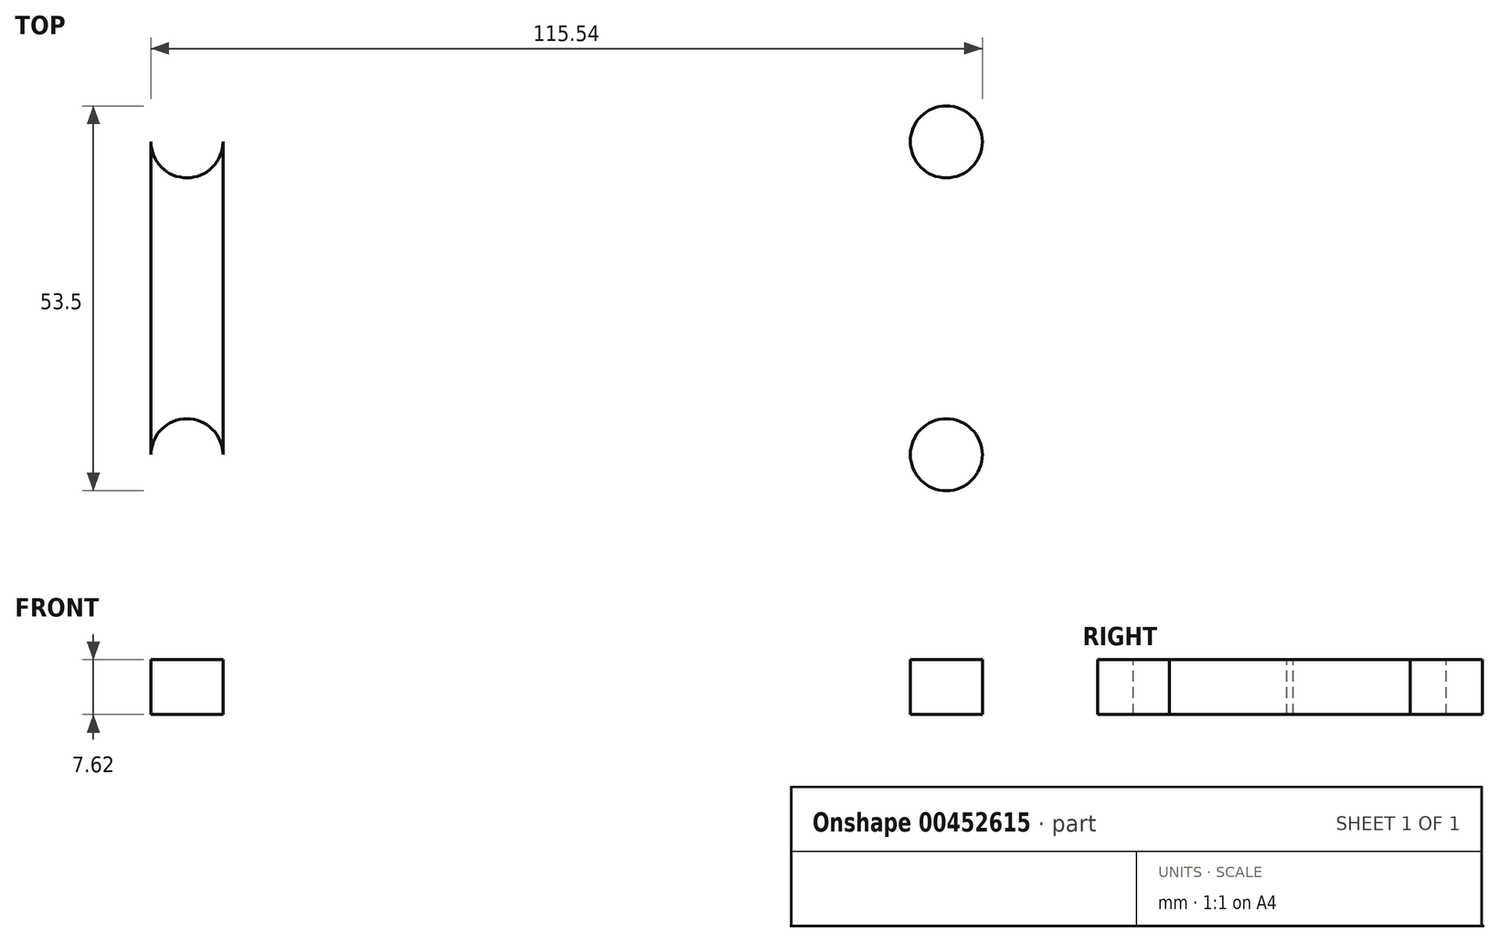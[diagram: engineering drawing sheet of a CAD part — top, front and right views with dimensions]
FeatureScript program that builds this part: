
annotation { "Feature Type Name" : "Feature", "Feature Type Description" : "" }
export const myFeature = defineFeature(function(context is Context, id is Id, definition is map)
    precondition{}
    {
        {
            var Q0;
            Q0=qCreatedBy(makeId("Top.planeOp"),FACE);
            var sketch = newSketch(context, id + "F0", { "sketchPlane" : qUnion([Q0])});
            skLineSegment(sketch, "E0.bottom", {"start": v(63.25, -31.75) * mm, "end": v(-63.25, -31.75) * mm});
            skLineSegment(sketch, "E0.top", {"start": v(63.25, 31.75) * mm, "end": v(-63.25, 31.75) * mm});
            skLineSegment(sketch, "E0.left", {"start": v(63.25, -31.75) * mm, "end": v(63.25, 31.75) * mm});
            skLineSegment(sketch, "E0.right", {"start": v(-63.25, -31.75) * mm, "end": v(-63.25, 31.75) * mm});
            skPoint(sketch, "E0.middle", {"position": v(0, 0) * mm});
            skLineSegment(sketch, "E1", {"start": v(0, 31.75) * mm, "end": v(0, -31.75) * mm, "construction": true});
            skLineSegment(sketch, "E2", {"start": v(-63.25, 0) * mm, "end": v(63.25, 0) * mm, "construction": true});
            skCircle(sketch, "E3", {"center": v(-27.5, 27.5) * mm, "radius": 2 * mm});
            skCircle(sketch, "E4.0.1.0", {"center": v(-27.5, -27.5) * mm, "radius": 2 * mm});
            skCircle(sketch, "E4.1.0.0", {"center": v(27.5, 27.5) * mm, "radius": 2 * mm});
            skCircle(sketch, "E4.1.1.0", {"center": v(27.5, -27.5) * mm, "radius": 2 * mm});
            skLineSegment(sketch, "E4.direction1", {"start": v(-27.5, 27.5) * mm, "end": v(27.5, 27.5) * mm, "construction": true});
            skLineSegment(sketch, "E4.direction2", {"start": v(-27.5, 27.5) * mm, "end": v(-27.5, -27.5) * mm, "construction": true});
            skCircle(sketch, "E5", {"center": v(0, 0) * mm, "radius": 26.94 * mm});
            skCircle(sketch, "E6", {"center": v(-62.75, 0) * mm, "radius": 5 * mm});
            skCircle(sketch, "E7", {"center": v(62.75, 0) * mm, "radius": 5 * mm});
            skCircle(sketch, "E8", {"center": v(-62.75, 0) * mm, "radius": 120.5 * mm});
            skCircle(sketch, "E9", {"center": v(-62.75, 0) * mm, "radius": 130.5 * mm});
            skCircle(sketch, "E10", {"center": v(-62.75, 0) * mm, "radius": 125.5 * mm});
            skCircle(sketch, "E11", {"center": v(60.77, 22.22) * mm, "radius": 5 * mm});
            skCircle(sketch, "E12", {"center": v(60.43, -24.02) * mm, "radius": 5 * mm});
            skCircle(sketch, "E13", {"center": v(-27.5, 27.5) * mm, "radius": 3.5 * mm});
            skCircle(sketch, "E14.MirrorC", {"center": v(27.5, 27.5) * mm, "radius": 3.5 * mm});
            skCircle(sketch, "E15.MirrorC", {"center": v(-27.5, -27.5) * mm, "radius": 3.5 * mm});
            skCircle(sketch, "E16.MirrorC", {"center": v(27.5, -27.5) * mm, "radius": 3.5 * mm});
            skSolve(sketch);
        }
        {
            var Q0;
            {var subQ0=sQuery(id+"F0.wireOp",EDGE,"E6");var subQ1=sQuery(id+"F0.wireOp",EDGE,"E0.right");var subQ2=makeQuery(id+"F0.imprint","INTERSECT",VERTEX,{"disambiguationData":[OD(0.0)],"derivedFrom":[subQ1,subQ0]});Q0=makeQuery(id+"F0.imprint","IMPRINT",FACE,{"disambiguationData":[TD([[makeQuery(id+"F0.imprint","IMPRINT",EDGE,{"disambiguationData":[TD([[subQ2,-1.0]])],"derivedFrom":subQ1}),-1.0]])]});}
            var Q1;
            {var subQ0=sQuery(id+"F0.wireOp",EDGE,"E6");var subQ1=sQuery(id+"F0.wireOp",EDGE,"E0.right");var subQ2=makeQuery(id+"F0.imprint","INTERSECT",VERTEX,{"disambiguationData":[OD(0.0)],"derivedFrom":[subQ1,subQ0]});Q1=makeQuery(id+"F0.imprint","IMPRINT",FACE,{"disambiguationData":[TD([[makeQuery(id+"F0.imprint","IMPRINT",EDGE,{"disambiguationData":[TD([[subQ2,-1.0]])],"derivedFrom":subQ1}),-1.0]])]});}
            var Q2;
            {var subQ0=sQuery(id+"F0.wireOp",EDGE,"E10");var subQ1=sQuery(id+"F0.wireOp",EDGE,"E0.top");var subQ2=makeQuery(id+"F0.imprint","INTERSECT",VERTEX,{"derivedFrom":[subQ1,subQ0]});Q2=makeQuery(id+"F0.imprint","IMPRINT",FACE,{"disambiguationData":[TD([[makeQuery(id+"F0.imprint","IMPRINT",EDGE,{"disambiguationData":[TD([[subQ2,-1.0]])],"derivedFrom":subQ1}),1.0]])]});}
            var Q3;
            {var subQ0=sQuery(id+"F0.wireOp",EDGE,"E0.left");var subQ1=sQuery(id+"F0.wireOp",EDGE,"E0.top");var subQ2=makeQuery(id+"F0.imprint","INTERSECT",VERTEX,{"derivedFrom":[subQ1,subQ0]});Q3=makeQuery(id+"F0.imprint","IMPRINT",FACE,{"disambiguationData":[TD([[makeQuery(id+"F0.imprint","IMPRINT",EDGE,{"disambiguationData":[TD([[subQ2,-1.0]])],"derivedFrom":subQ1}),1.0]])]});}
            var Q4;
            {var subQ0=sQuery(id+"F0.wireOp",EDGE,"E10");var subQ1=sQuery(id+"F0.wireOp",EDGE,"E0.top");var subQ2=makeQuery(id+"F0.imprint","INTERSECT",VERTEX,{"derivedFrom":[subQ1,subQ0]});Q4=makeQuery(id+"F0.imprint","IMPRINT",FACE,{"disambiguationData":[TD([[makeQuery(id+"F0.imprint","IMPRINT",EDGE,{"disambiguationData":[TD([[subQ2,-1.0]])],"derivedFrom":subQ1}),1.0]])]});}
            var Q5;
            {var subQ0=sQuery(id+"F0.wireOp",EDGE,"E0.left");var subQ1=sQuery(id+"F0.wireOp",EDGE,"E0.bottom");var subQ2=makeQuery(id+"F0.imprint","INTERSECT",VERTEX,{"derivedFrom":[subQ1,subQ0]});Q5=makeQuery(id+"F0.imprint","IMPRINT",FACE,{"disambiguationData":[TD([[makeQuery(id+"F0.imprint","IMPRINT",EDGE,{"disambiguationData":[TD([[subQ2,-1.0]])],"derivedFrom":subQ1}),-1.0]])]});}
            var Q6;
            {var subQ0=sQuery(id+"F0.wireOp",EDGE,"E0.left");var subQ1=sQuery(id+"F0.wireOp",EDGE,"E0.top");var subQ2=makeQuery(id+"F0.imprint","INTERSECT",VERTEX,{"derivedFrom":[subQ1,subQ0]});Q6=makeQuery(id+"F0.imprint","IMPRINT",FACE,{"disambiguationData":[TD([[makeQuery(id+"F0.imprint","IMPRINT",EDGE,{"disambiguationData":[TD([[subQ2,-1.0]])],"derivedFrom":subQ1}),1.0]])]});}
            var Q7;
            {var subQ0=sQuery(id+"F0.wireOp",EDGE,"E12");var subQ1=sQuery(id+"F0.wireOp",EDGE,"E0.left");var subQ2=makeQuery(id+"F0.imprint","INTERSECT",VERTEX,{"disambiguationData":[OD(0.0)],"derivedFrom":[subQ1,subQ0]});Q7=makeQuery(id+"F0.imprint","IMPRINT",FACE,{"disambiguationData":[TD([[makeQuery(id+"F0.imprint","IMPRINT",EDGE,{"disambiguationData":[TD([[subQ2,-1.0]])],"derivedFrom":subQ1}),1.0]])]});}
            var Q8;
            {var subQ0=sQuery(id+"F0.wireOp",EDGE,"E12");var subQ1=sQuery(id+"F0.wireOp",EDGE,"E0.left");var subQ2=makeQuery(id+"F0.imprint","INTERSECT",VERTEX,{"disambiguationData":[OD(1.0)],"derivedFrom":[subQ1,subQ0]});Q8=makeQuery(id+"F0.imprint","IMPRINT",FACE,{"disambiguationData":[TD([[makeQuery(id+"F0.imprint","IMPRINT",EDGE,{"disambiguationData":[TD([[subQ2,-1.0]])],"derivedFrom":subQ1}),1.0]])]});}
            var Q9;
            {var subQ0=sQuery(id+"F0.wireOp",EDGE,"E7");var subQ1=sQuery(id+"F0.wireOp",EDGE,"E0.left");var subQ2=makeQuery(id+"F0.imprint","INTERSECT",VERTEX,{"disambiguationData":[OD(0.0)],"derivedFrom":[subQ1,subQ0]});Q9=makeQuery(id+"F0.imprint","IMPRINT",FACE,{"disambiguationData":[TD([[makeQuery(id+"F0.imprint","IMPRINT",EDGE,{"disambiguationData":[TD([[subQ2,-1.0]])],"derivedFrom":subQ1}),1.0]])]});}
            var Q10;
            {var subQ0=sQuery(id+"F0.wireOp",EDGE,"E7");var subQ1=sQuery(id+"F0.wireOp",EDGE,"E0.left");var subQ2=makeQuery(id+"F0.imprint","INTERSECT",VERTEX,{"disambiguationData":[OD(1.0)],"derivedFrom":[subQ1,subQ0]});Q10=makeQuery(id+"F0.imprint","IMPRINT",FACE,{"disambiguationData":[TD([[makeQuery(id+"F0.imprint","IMPRINT",EDGE,{"disambiguationData":[TD([[subQ2,-1.0]])],"derivedFrom":subQ1}),1.0]])]});}
            var Q11;
            {var subQ0=sQuery(id+"F0.wireOp",EDGE,"E11");var subQ1=sQuery(id+"F0.wireOp",EDGE,"E0.left");var subQ2=makeQuery(id+"F0.imprint","INTERSECT",VERTEX,{"disambiguationData":[OD(0.0)],"derivedFrom":[subQ1,subQ0]});Q11=makeQuery(id+"F0.imprint","IMPRINT",FACE,{"disambiguationData":[TD([[makeQuery(id+"F0.imprint","IMPRINT",EDGE,{"disambiguationData":[TD([[subQ2,-1.0]])],"derivedFrom":subQ1}),1.0]])]});}
            var Q12;
            {var subQ0=sQuery(id+"F0.wireOp",EDGE,"E0.left");var subQ1=sQuery(id+"F0.wireOp",EDGE,"E0.bottom");var subQ2=makeQuery(id+"F0.imprint","INTERSECT",VERTEX,{"derivedFrom":[subQ1,subQ0]});Q12=makeQuery(id+"F0.imprint","IMPRINT",FACE,{"disambiguationData":[TD([[makeQuery(id+"F0.imprint","IMPRINT",EDGE,{"disambiguationData":[TD([[subQ2,-1.0]])],"derivedFrom":subQ1}),-1.0]])]});}
            var Q13;
            {var subQ0=sQuery(id+"F0.wireOp",EDGE,"E10");var subQ1=sQuery(id+"F0.wireOp",EDGE,"E0.bottom");var subQ2=makeQuery(id+"F0.imprint","INTERSECT",VERTEX,{"derivedFrom":[subQ1,subQ0]});Q13=makeQuery(id+"F0.imprint","IMPRINT",FACE,{"disambiguationData":[TD([[makeQuery(id+"F0.imprint","IMPRINT",EDGE,{"disambiguationData":[TD([[subQ2,-1.0]])],"derivedFrom":subQ1}),-1.0]])]});}
            var Q14;
            {var subQ0=sQuery(id+"F0.wireOp",EDGE,"E10");var subQ1=sQuery(id+"F0.wireOp",EDGE,"E0.bottom");var subQ2=makeQuery(id+"F0.imprint","INTERSECT",VERTEX,{"derivedFrom":[subQ1,subQ0]});Q14=makeQuery(id+"F0.imprint","IMPRINT",FACE,{"disambiguationData":[TD([[makeQuery(id+"F0.imprint","IMPRINT",EDGE,{"disambiguationData":[TD([[subQ2,-1.0]])],"derivedFrom":subQ1}),-1.0]])]});}
            var Q15;
            Q15=makeQuery(id+"F0.imprint","IMPRINT",FACE,{"disambiguationData":[TD([[makeQuery(id+"F0.imprint","IMPRINT",EDGE,{"derivedFrom":sQuery(id+"F0.wireOp",EDGE,"E4.0.1.0")}),-1.0]])]});
            var Q16;
            Q16=makeQuery(id+"F0.imprint","IMPRINT",FACE,{"disambiguationData":[TD([[makeQuery(id+"F0.imprint","IMPRINT",EDGE,{"derivedFrom":sQuery(id+"F0.wireOp",EDGE,"E3")}),-1.0]])]});
            var Q17;
            Q17=makeQuery(id+"F0.imprint","IMPRINT",FACE,{"disambiguationData":[TD([[makeQuery(id+"F0.imprint","IMPRINT",EDGE,{"derivedFrom":sQuery(id+"F0.wireOp",EDGE,"E4.1.0.0")}),-1.0]])]});
            var Q18;
            Q18=makeQuery(id+"F0.imprint","IMPRINT",FACE,{"disambiguationData":[TD([[makeQuery(id+"F0.imprint","IMPRINT",EDGE,{"derivedFrom":sQuery(id+"F0.wireOp",EDGE,"E4.1.1.0")}),-1.0]])]});
            var Q19;
            {var subQ0=sQuery(id+"F0.wireOp",EDGE,"E11");var subQ1=sQuery(id+"F0.wireOp",EDGE,"E10");var subQ2=makeQuery(id+"F0.imprint","INTERSECT",VERTEX,{"disambiguationData":[OD(0.0)],"derivedFrom":[subQ1,subQ0]});Q19=makeQuery(id+"F0.imprint","IMPRINT",FACE,{"disambiguationData":[TD([[makeQuery(id+"F0.imprint","IMPRINT",EDGE,{"disambiguationData":[TD([[subQ2,-1.0]])],"derivedFrom":subQ1}),1.0]])]});}
            var Q20;
            {var subQ0=sQuery(id+"F0.wireOp",EDGE,"E11");var subQ1=sQuery(id+"F0.wireOp",EDGE,"E0.left");var subQ2=makeQuery(id+"F0.imprint","INTERSECT",VERTEX,{"disambiguationData":[OD(0.0)],"derivedFrom":[subQ1,subQ0]});Q20=makeQuery(id+"F0.imprint","IMPRINT",FACE,{"disambiguationData":[TD([[makeQuery(id+"F0.imprint","IMPRINT",EDGE,{"disambiguationData":[TD([[subQ2,-1.0]])],"derivedFrom":subQ1}),1.0]])]});}
            var Q21;
            {var subQ0=sQuery(id+"F0.wireOp",EDGE,"E10");var subQ1=sQuery(id+"F0.wireOp",EDGE,"E7");var subQ2=makeQuery(id+"F0.imprint","INTERSECT",VERTEX,{"disambiguationData":[OD(0.0)],"derivedFrom":[subQ1,subQ0]});Q21=makeQuery(id+"F0.imprint","IMPRINT",FACE,{"disambiguationData":[TD([[makeQuery(id+"F0.imprint","IMPRINT",EDGE,{"disambiguationData":[TD([[subQ2,-1.0]])],"derivedFrom":subQ1}),-1.0]])]});}
            var Q22;
            {var subQ0=sQuery(id+"F0.wireOp",EDGE,"E7");var subQ1=sQuery(id+"F0.wireOp",EDGE,"E0.left");var subQ2=makeQuery(id+"F0.imprint","INTERSECT",VERTEX,{"disambiguationData":[OD(1.0)],"derivedFrom":[subQ1,subQ0]});Q22=makeQuery(id+"F0.imprint","IMPRINT",FACE,{"disambiguationData":[TD([[makeQuery(id+"F0.imprint","IMPRINT",EDGE,{"disambiguationData":[TD([[subQ2,-1.0]])],"derivedFrom":subQ1}),1.0]])]});}
            var Q23;
            {var subQ0=sQuery(id+"F0.wireOp",EDGE,"E10");var subQ1=sQuery(id+"F0.wireOp",EDGE,"E7");var subQ2=makeQuery(id+"F0.imprint","INTERSECT",VERTEX,{"disambiguationData":[OD(0.0)],"derivedFrom":[subQ1,subQ0]});Q23=makeQuery(id+"F0.imprint","IMPRINT",FACE,{"disambiguationData":[TD([[makeQuery(id+"F0.imprint","IMPRINT",EDGE,{"disambiguationData":[TD([[subQ2,-1.0]])],"derivedFrom":subQ1}),1.0]])]});}
            var Q24;
            {var subQ0=sQuery(id+"F0.wireOp",EDGE,"E7");var subQ1=sQuery(id+"F0.wireOp",EDGE,"E0.left");var subQ2=makeQuery(id+"F0.imprint","INTERSECT",VERTEX,{"disambiguationData":[OD(0.0)],"derivedFrom":[subQ1,subQ0]});Q24=makeQuery(id+"F0.imprint","IMPRINT",FACE,{"disambiguationData":[TD([[makeQuery(id+"F0.imprint","IMPRINT",EDGE,{"disambiguationData":[TD([[subQ2,-1.0]])],"derivedFrom":subQ1}),1.0]])]});}
            var Q25;
            {var subQ0=sQuery(id+"F0.wireOp",EDGE,"E8");var subQ1=sQuery(id+"F0.wireOp",EDGE,"E7");var subQ2=makeQuery(id+"F0.imprint","INTERSECT",VERTEX,{"derivedFrom":[subQ1,subQ0]});Q25=makeQuery(id+"F0.imprint","IMPRINT",FACE,{"disambiguationData":[TD([[makeQuery(id+"F0.imprint","IMPRINT",EDGE,{"disambiguationData":[TD([[subQ2,-1.0]])],"derivedFrom":subQ1}),-1.0]])]});}
            var Q26;
            {var subQ0=sQuery(id+"F0.wireOp",EDGE,"E12");var subQ1=sQuery(id+"F0.wireOp",EDGE,"E10");var subQ2=makeQuery(id+"F0.imprint","INTERSECT",VERTEX,{"disambiguationData":[OD(0.0)],"derivedFrom":[subQ1,subQ0]});Q26=makeQuery(id+"F0.imprint","IMPRINT",FACE,{"disambiguationData":[TD([[makeQuery(id+"F0.imprint","IMPRINT",EDGE,{"disambiguationData":[TD([[subQ2,-1.0]])],"derivedFrom":subQ1}),1.0]])]});}
            var Q27;
            {var subQ0=sQuery(id+"F0.wireOp",EDGE,"E12");var subQ1=sQuery(id+"F0.wireOp",EDGE,"E0.left");var subQ2=makeQuery(id+"F0.imprint","INTERSECT",VERTEX,{"disambiguationData":[OD(0.0)],"derivedFrom":[subQ1,subQ0]});Q27=makeQuery(id+"F0.imprint","IMPRINT",FACE,{"disambiguationData":[TD([[makeQuery(id+"F0.imprint","IMPRINT",EDGE,{"disambiguationData":[TD([[subQ2,-1.0]])],"derivedFrom":subQ1}),1.0]])]});}
            var Q28;
            Q28=makeQuery(id+"F0.imprint","IMPRINT",FACE,{"disambiguationData":[TD([[makeQuery(id+"F0.imprint","IMPRINT",EDGE,{"derivedFrom":sQuery(id+"F0.wireOp",EDGE,"E5")}),-1.0]])]});
            extrude(context, id + "F1", {"entities" : qUnion([Q0, Q1, Q2, Q3, Q4, Q5, Q6, Q7, Q8, Q9, Q10, Q11, Q12, Q13, Q14, Q15, Q16, Q17, Q18, Q19, Q20, Q21, Q22, Q23, Q24, Q25, Q26, Q27, Q28]), "depth" : 7.62 * mm});
        }
        {
            var Q0;
            Q0=makeQuery(id+"F1.opExtrude","SWEPT_EDGE",EDGE,{"disambiguationData":[OSD([sQuery(id+"F0.wireOp",EDGE,"E0.top"),sQuery(id+"F0.wireOp",EDGE,"E0.right")])]});
            var Q1;
            Q1=makeQuery(id+"F1.opExtrude","SWEPT_EDGE",EDGE,{"disambiguationData":[OSD([sQuery(id+"F0.wireOp",EDGE,"E0.bottom"),sQuery(id+"F0.wireOp",EDGE,"E0.right")])]});
            var Q2;
            Q2=makeQuery(id+"F1.opExtrude","SWEPT_EDGE",EDGE,{"disambiguationData":[OSD([sQuery(id+"F0.wireOp",EDGE,"E0.top"),sQuery(id+"F0.wireOp",EDGE,"E0.left")])]});
            var Q3;
            Q3=makeQuery(id+"F1.opExtrude","SWEPT_EDGE",EDGE,{"disambiguationData":[OSD([sQuery(id+"F0.wireOp",EDGE,"E0.bottom"),sQuery(id+"F0.wireOp",EDGE,"E0.left")])]});
            chamfer(context, id + "F2", {"entities" : qUnion([Q0, Q1, Q2, Q3]), "width" : 5 * mm, "tangentPropagation" : true});
        }
        {
            var Q0;
            Q0=makeQuery(id+"F0.imprint","IMPRINT",FACE,{"disambiguationData":[TD([[makeQuery(id+"F0.imprint","IMPRINT",EDGE,{"derivedFrom":sQuery(id+"F0.wireOp",EDGE,"E4.0.1.0")}),-1.0]])]});
            var Q1;
            Q1=makeQuery(id+"F0.imprint","IMPRINT",FACE,{"disambiguationData":[TD([[makeQuery(id+"F0.imprint","IMPRINT",EDGE,{"derivedFrom":sQuery(id+"F0.wireOp",EDGE,"E4.1.1.0")}),-1.0]])]});
            var Q2;
            Q2=makeQuery(id+"F0.imprint","IMPRINT",FACE,{"disambiguationData":[TD([[makeQuery(id+"F0.imprint","IMPRINT",EDGE,{"derivedFrom":sQuery(id+"F0.wireOp",EDGE,"E3")}),-1.0]])]});
            var Q3;
            Q3=makeQuery(id+"F0.imprint","IMPRINT",FACE,{"disambiguationData":[TD([[makeQuery(id+"F0.imprint","IMPRINT",EDGE,{"derivedFrom":sQuery(id+"F0.wireOp",EDGE,"E4.1.0.0")}),-1.0]])]});
            extrude(context, id + "F3", {"entities" : qUnion([Q0, Q1, Q2, Q3]), "operationType" : NewBodyOperationType.REMOVE, "depth" : 3 * mm});
        }
        {
            var Q0;
            Q0=makeQuery(id+"F1.opExtrude","CAP_FACE",FACE,{"disambiguationData":[OSD([sQuery(id+"F0.wireOp",EDGE,"E0.bottom"),sQuery(id+"F0.wireOp",EDGE,"E0.top"),sQuery(id+"F0.wireOp",EDGE,"E0.left"),sQuery(id+"F0.wireOp",EDGE,"E0.right"),sQuery(id+"F0.wireOp",EDGE,"E3"),sQuery(id+"F0.wireOp",EDGE,"E4.0.1.0"),sQuery(id+"F0.wireOp",EDGE,"E4.1.0.0"),sQuery(id+"F0.wireOp",EDGE,"E4.1.1.0"),sQuery(id+"F0.wireOp",EDGE,"E5")])],"isStart":false});
            var sketch = newSketch(context, id + "F4", { "sketchPlane" : qUnion([Q0])});
            skPoint(sketch, "E17", {"position": v(-52.77, 0) * mm});
            skLineSegment(sketch, "E18", {"start": v(-52.77, 0) * mm, "end": v(0, 0) * mm, "construction": true});
            skCircle(sketch, "E19", {"center": v(-52.77, 0) * mm, "radius": 5 * mm});
            skLineSegment(sketch, "E20", {"start": v(0, 31.75) * mm, "end": v(0, -31.75) * mm, "construction": true});
            skLineSegment(sketch, "E21", {"start": v(-52.77, 0) * mm, "end": v(-52.77, 31.75) * mm, "construction": true});
            skLineSegment(sketch, "E22", {"start": v(-52.77, 0) * mm, "end": v(-52.77, -31.75) * mm, "construction": true});
            skLineSegment(sketch, "E23.bottom", {"start": v(-57.77, 21.75) * mm, "end": v(-47.77, 21.75) * mm});
            skLineSegment(sketch, "E23.top", {"start": v(-57.77, -21.75) * mm, "end": v(-47.77, -21.75) * mm});
            skLineSegment(sketch, "E23.left", {"start": v(-57.77, 21.75) * mm, "end": v(-57.77, -21.75) * mm});
            skLineSegment(sketch, "E23.right", {"start": v(-47.77, 21.75) * mm, "end": v(-47.77, -21.75) * mm});
            skCircle(sketch, "E24", {"center": v(-52.77, 21.75) * mm, "radius": 5 * mm});
            skCircle(sketch, "E25", {"center": v(-52.77, -21.75) * mm, "radius": 5 * mm});
            skCircle(sketch, "E26.MirrorC", {"center": v(52.77, 21.75) * mm, "radius": 5 * mm});
            skLineSegment(sketch, "E27.MirrorCS", {"start": v(57.77, 21.75) * mm, "end": v(57.77, -21.75) * mm});
            skCircle(sketch, "E28.MirrorC", {"center": v(52.77, -21.75) * mm, "radius": 5 * mm});
            skLineSegment(sketch, "E29.MirrorCS", {"start": v(47.77, 21.75) * mm, "end": v(47.77, -21.75) * mm});
            skLineSegment(sketch, "E30", {"start": v(52.77, 21.75) * mm, "end": v(52.77, -21.75) * mm, "construction": true});
            skLineSegment(sketch, "E31", {"start": v(47.77, 0) * mm, "end": v(57.77, 0) * mm, "construction": true});
            skPoint(sketch, "E32", {"position": v(52.77, 0) * mm});
            skSolve(sketch);
        }
        {
            var Q0;
            {var subQ0=sQuery(id+"F4.wireOp",EDGE,"E23.left");var subQ1=sQuery(id+"F4.wireOp",EDGE,"E19");var subQ2=makeQuery(id+"F4.imprint","INTERSECT",VERTEX,{"derivedFrom":[subQ1,subQ0]});Q0=makeQuery(id+"F4.imprint","IMPRINT",FACE,{"disambiguationData":[TD([[makeQuery(id+"F4.imprint","IMPRINT",EDGE,{"disambiguationData":[TD([[subQ2,-1.0]])],"derivedFrom":subQ1}),-1.0]])]});}
            var Q1;
            {var subQ0=sQuery(id+"F4.wireOp",EDGE,"E19");var subQ1=makeQuery(id+"F4.imprint","INTERSECT",VERTEX,{"derivedFrom":[subQ0,sQuery(id+"F4.wireOp",EDGE,"E23.left")]});Q1=makeQuery(id+"F4.imprint","IMPRINT",FACE,{"disambiguationData":[TD([[makeQuery(id+"F4.imprint","IMPRINT",EDGE,{"disambiguationData":[TD([[subQ1,1.0]])],"derivedFrom":subQ0}),1.0]])]});}
            var Q2;
            {var subQ0=sQuery(id+"F4.wireOp",EDGE,"E23.left");var subQ1=sQuery(id+"F4.wireOp",EDGE,"E19");var subQ2=makeQuery(id+"F4.imprint","INTERSECT",VERTEX,{"derivedFrom":[subQ1,subQ0]});Q2=makeQuery(id+"F4.imprint","IMPRINT",FACE,{"disambiguationData":[TD([[makeQuery(id+"F4.imprint","IMPRINT",EDGE,{"disambiguationData":[TD([[subQ2,1.0]])],"derivedFrom":subQ1}),-1.0]])]});}
            var Q3;
            {var subQ0=sQuery(id+"F4.wireOp",EDGE,"E23.bottom");Q3=makeQuery(id+"F4.imprint","IMPRINT",FACE,{"disambiguationData":[TD([[makeQuery(id+"F4.imprint","IMPRINT",EDGE,{"derivedFrom":subQ0}),-1.0]])]});}
            var Q4;
            {var subQ0=sQuery(id+"F4.wireOp",EDGE,"E23.bottom");Q4=makeQuery(id+"F4.imprint","IMPRINT",FACE,{"disambiguationData":[TD([[makeQuery(id+"F4.imprint","IMPRINT",EDGE,{"derivedFrom":subQ0}),1.0]])]});}
            var Q5;
            {var subQ0=sQuery(id+"F4.wireOp",EDGE,"E23.top");Q5=makeQuery(id+"F4.imprint","IMPRINT",FACE,{"disambiguationData":[TD([[makeQuery(id+"F4.imprint","IMPRINT",EDGE,{"derivedFrom":subQ0}),1.0]])]});}
            var Q6;
            {var subQ0=sQuery(id+"F4.wireOp",EDGE,"E23.top");Q6=makeQuery(id+"F4.imprint","IMPRINT",FACE,{"disambiguationData":[TD([[makeQuery(id+"F4.imprint","IMPRINT",EDGE,{"derivedFrom":subQ0}),-1.0]])]});}
            var Q7;
            {var subQ0=sQuery(id+"F4.wireOp",EDGE,"E28.MirrorC");var subQ1=makeQuery(id+"F4.imprint","INTERSECT",VERTEX,{"derivedFrom":[sQuery(id+"F4.wireOp",EDGE,"E27.MirrorCS"),subQ0]});Q7=makeQuery(id+"F4.imprint","IMPRINT",FACE,{"disambiguationData":[TD([[makeQuery(id+"F4.imprint","IMPRINT",EDGE,{"disambiguationData":[TD([[subQ1,1.0]])],"derivedFrom":subQ0}),-1.0]])]});}
            var Q8;
            {var subQ0=sQuery(id+"F4.wireOp",EDGE,"E27.MirrorCS");Q8=makeQuery(id+"F4.imprint","IMPRINT",FACE,{"disambiguationData":[TD([[makeQuery(id+"F4.imprint","IMPRINT",EDGE,{"derivedFrom":subQ0}),-1.0]])]});}
            var Q9;
            {var subQ0=sQuery(id+"F4.wireOp",EDGE,"E26.MirrorC");var subQ1=makeQuery(id+"F4.imprint","INTERSECT",VERTEX,{"derivedFrom":[subQ0,sQuery(id+"F4.wireOp",EDGE,"E27.MirrorCS")]});Q9=makeQuery(id+"F4.imprint","IMPRINT",FACE,{"disambiguationData":[TD([[makeQuery(id+"F4.imprint","IMPRINT",EDGE,{"disambiguationData":[TD([[subQ1,1.0]])],"derivedFrom":subQ0}),-1.0]])]});}
            extrude(context, id + "F5", {"entities" : qUnion([Q0, Q1, Q2, Q3, Q4, Q5, Q6, Q7, Q8, Q9]), "operationType" : NewBodyOperationType.REMOVE, "endBound" : BoundingType.THROUGH_ALL, "oppositeDirection" : true, "depth" : 25 * mm});
        }
    });
